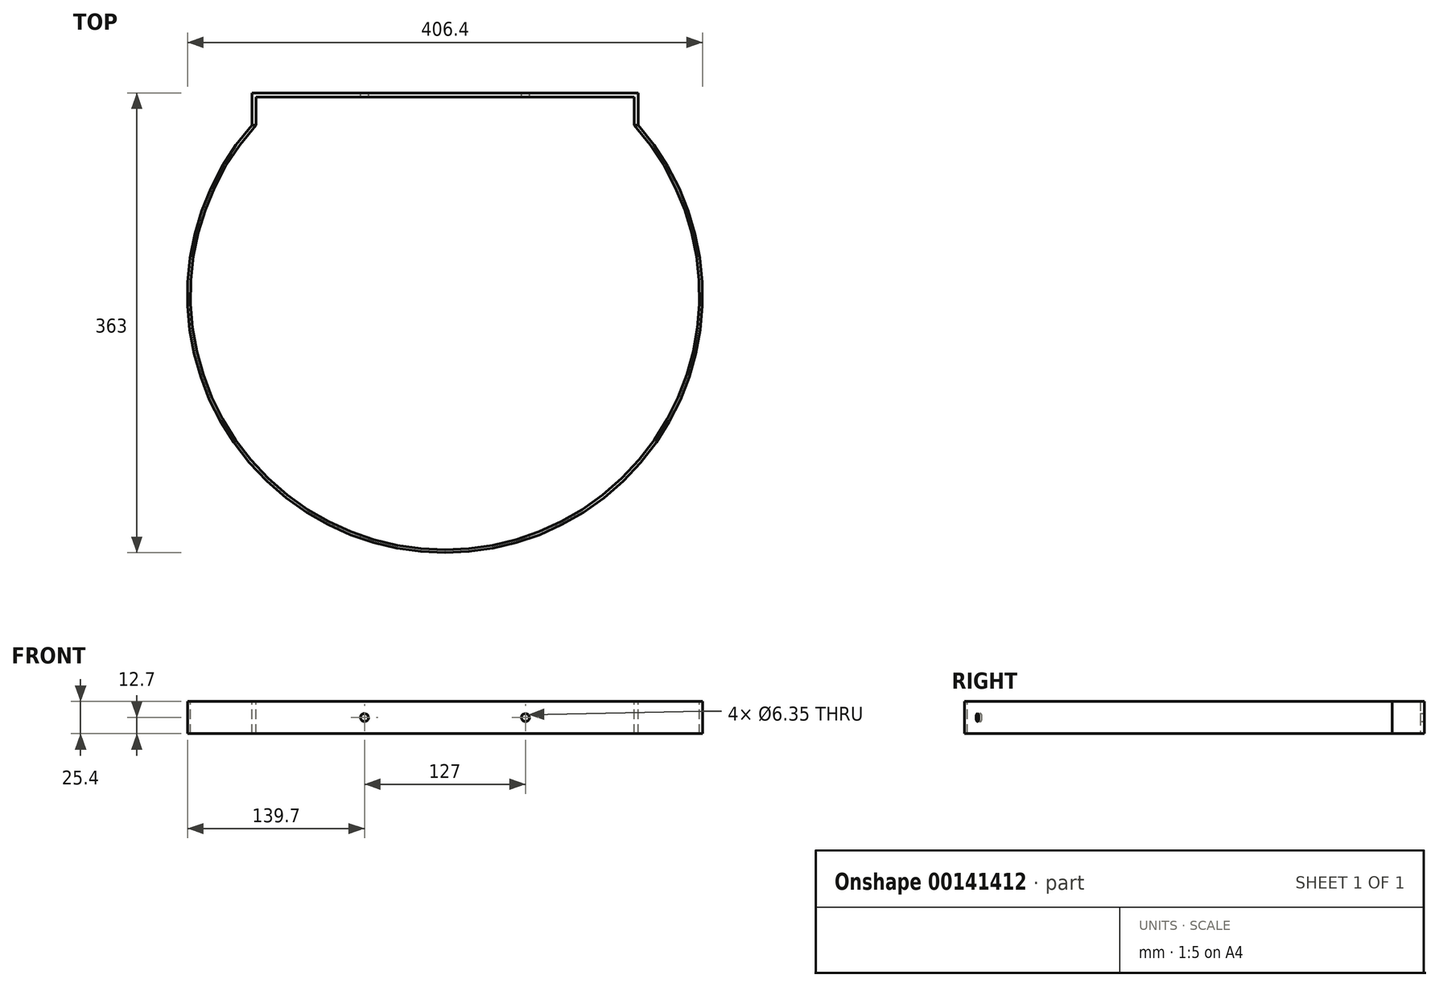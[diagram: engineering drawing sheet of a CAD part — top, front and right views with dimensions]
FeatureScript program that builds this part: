
annotation { "Feature Type Name" : "Feature", "Feature Type Description" : "" }
export const myFeature = defineFeature(function(context is Context, id is Id, definition is map)
    precondition{}
    {
        {
            var Q0;
            Q0=qCreatedBy(makeId("Top.planeOp"),FACE);
            var sketch = newSketch(context, id + "F0", { "sketchPlane" : qUnion([Q0])});
            skLineSegment(sketch, "E0", {"start": v(-152.4, 0) * mm, "end": v(152.4, 0) * mm});
            skLineSegment(sketch, "E1", {"start": v(-152.4, 0) * mm, "end": v(-152.4, -25.4) * mm});
            skLineSegment(sketch, "E2", {"start": v(-149.22, -25.4) * mm, "end": v(-149.22, -3.18) * mm});
            skLineSegment(sketch, "E3", {"start": v(-149.22, -3.18) * mm, "end": v(149.22, -3.18) * mm});
            skLineSegment(sketch, "E4", {"start": v(149.22, -3.18) * mm, "end": v(149.22, -25.4) * mm});
            skLineSegment(sketch, "E5", {"start": v(152.4, -25.4) * mm, "end": v(152.4, 0) * mm});
            skLineSegment(sketch, "E6", {"start": v(-152.4, -25.4) * mm, "end": v(-149.22, -25.4) * mm});
            skLineSegment(sketch, "E7", {"start": v(149.22, -25.4) * mm, "end": v(152.4, -25.4) * mm});
            skSolve(sketch);
        }
        {
            var Q0;
            Q0 = qSketchRegion(id + "F0", true);
            extrude(context, id + "F1", {"entities" : qUnion([Q0]), "depth" : 25.4 * mm});
        }
        {
            var Q0;
            Q0=makeQuery(id+"F1.opExtrude","CAP_FACE",FACE,{"disambiguationData":[OSD([sQuery(id+"F0.wireOp",EDGE,"E0"),sQuery(id+"F0.wireOp",EDGE,"E1"),sQuery(id+"F0.wireOp",EDGE,"E2"),sQuery(id+"F0.wireOp",EDGE,"E3"),sQuery(id+"F0.wireOp",EDGE,"E4"),sQuery(id+"F0.wireOp",EDGE,"E5"),sQuery(id+"F0.wireOp",EDGE,"E6"),sQuery(id+"F0.wireOp",EDGE,"E7")])],"isStart":false});
            var sketch = newSketch(context, id + "F2", { "sketchPlane" : qUnion([Q0])});
            skArc(sketch, "E8", {"start": v(-152.4, -25.4) * mm, "mid": v(0, -363) * mm, "end": v(152.4, -25.4) * mm});
            skArc(sketch, "E9", {"start": v(-149.23, -25.4) * mm, "mid": v(0, -360.63) * mm, "end": v(149.23, -25.4) * mm});
            skSolve(sketch);
        }
        {
            var Q0;
            Q0 = qSketchRegion(id + "F2", true);
            var Q1;
            Q1=makeQuery(id+"F2.imprint","IMPRINT",FACE,{"disambiguationData":[TD([[makeQuery(id+"F2.imprint","IMPRINT",EDGE,{"derivedFrom":sQuery(id+"F2.wireOp",EDGE,"E8")}),1.0]])]});
            extrude(context, id + "F3", {"entities" : qUnion([Q0, Q1]), "oppositeDirection" : true, "depth" : 25.4 * mm});
        }
        {
            var Q0;
            Q0=makeQuery(id+"F1.opExtrude","SWEPT_FACE",FACE,{"disambiguationData":[OSD([sQuery(id+"F0.wireOp",EDGE,"E0")])]});
            var sketch = newSketch(context, id + "F4", { "sketchPlane" : qUnion([Q0])});
            skLineSegment(sketch, "E10", {"start": v(-152.4, 12.7) * mm, "end": v(152.4, 12.7) * mm});
            skCircle(sketch, "E11", {"center": v(-63.5, 12.7) * mm, "radius": 3.18 * mm});
            skCircle(sketch, "E12", {"center": v(63.5, 12.7) * mm, "radius": 3.18 * mm});
            skSolve(sketch);
        }
        {
            var Q0;
            Q0 = qSketchRegion(id + "F4", true);
            extrude(context, id + "F5", {"entities" : qUnion([Q0]), "operationType" : NewBodyOperationType.REMOVE, "endBound" : BoundingType.THROUGH_ALL, "oppositeDirection" : true, "depth" : 25.4 * mm});
        }
    });
